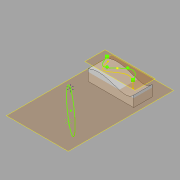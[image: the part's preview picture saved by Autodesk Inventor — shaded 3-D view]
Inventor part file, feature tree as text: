
AUTODESK INVENTOR PART (.ipt)
format: ipt  version: 2017.2 (Build 212233000, 233)  size: 110,592 bytes
history: native  units: mm
features: sketch x6, extrude x1, plane x1, other x1
ambient origin geometry x8: Origin, YZ Plane, XZ Plane, XY Plane, X Axis, Y Axis, Z Axis, Center Point
bodies: Solid1 (feature_tree)
feature tree (9):
  extrude  "Extrusion1"  Depth=4.5mm
  plane  "Work Plane1"
  sketch  "Sketch2"
  sketch  "3D Sketch1"
  sketch  "3D Sketch6"
  sketch  "3D Sketch7"
  sketch  "3D Sketch5"
  sketch  "Sketch1"  dims[d0=10.0mm d1=0.0mm d2=4.5mm]
  other  "Project to Surface1"
